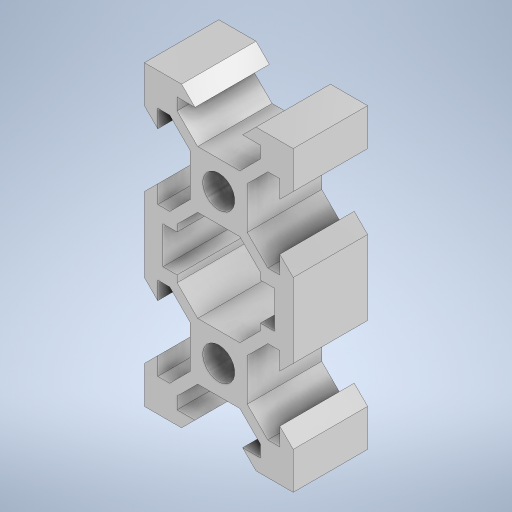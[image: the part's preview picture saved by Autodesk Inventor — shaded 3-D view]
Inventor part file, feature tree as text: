
AUTODESK INVENTOR PART (.ipt)
format: ipt  version: 2024.2 (Build 282272000, 272)  size: 398,336 bytes
history: native  units: mm
features: extrude x2, sketch x2, pattern_linear x1
ambient origin geometry x8: Origin, YZ Plane, XZ Plane, XY Plane, X Axis, Y Axis, Z Axis, Center Point
bodies: Solid1 (feature_tree)
feature tree (5):
  extrude  "Extrusion1"  Depth=10.0mm
  pattern_linear  "Rectangular Pattern1"  Spacing1=4.4mm  [1 undecoded]
  extrude  "Extrusion2"  TaperAngle=45.0deg  [1 undecoded]
  sketch  "Sketch1"  dims[d16=10.0mm d19=3.2mm]
  sketch  "Sketch2"  dims[d21=4.4mm d22=4.4mm d24=45.0deg d25=1.8mm d27=1.8mm d28=45.0deg d29=3.2mm d31=1.4mm d33=2.15mm d34=3.825mm d35=3.825mm d36=135.0deg d37=40.0mm d39=360.0deg d41=10.0mm d42=0.0mm d43=20.0mm d45=20.0mm d46=5.0mm d47=15.0mm d48=0.0mm d49=0.0mm]
note: 2 required parameter values undecoded (feature->parameter linkage not recoverable at this tier; creation-order binding heuristic only, values carry confidence <= 0.55)
